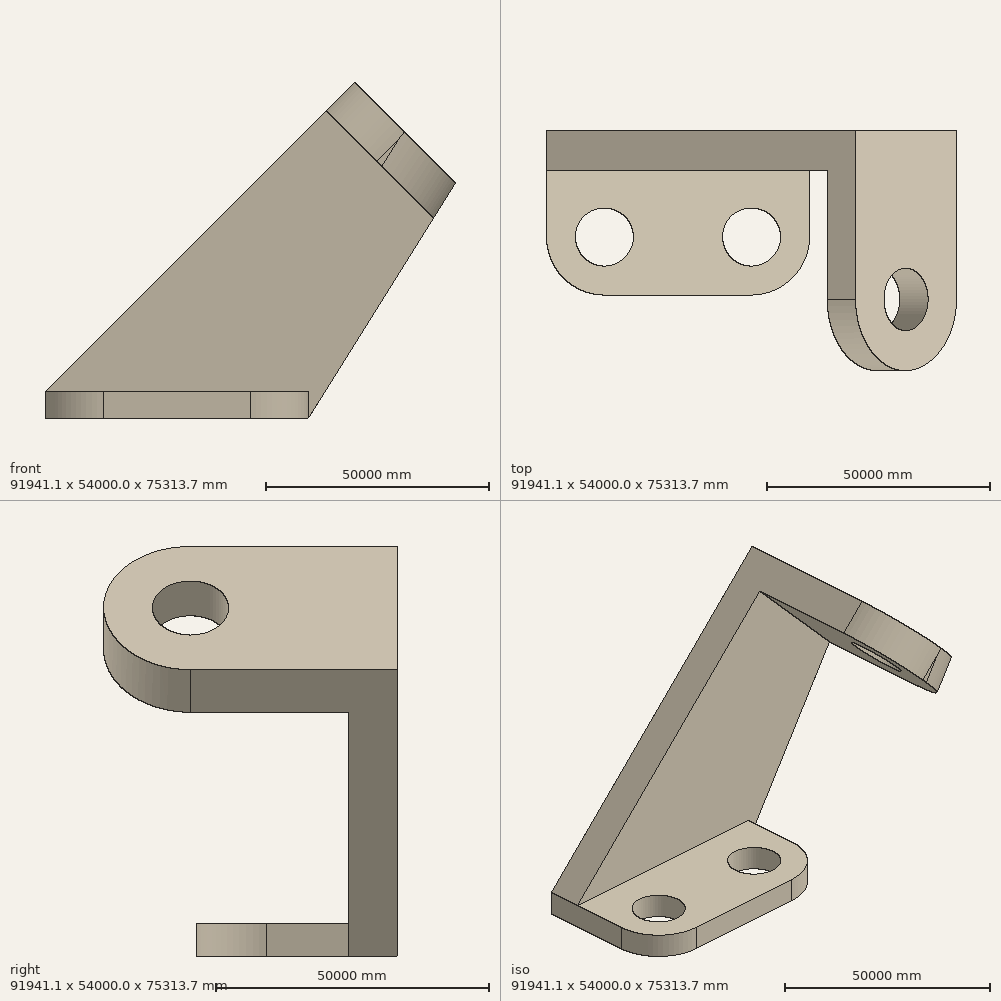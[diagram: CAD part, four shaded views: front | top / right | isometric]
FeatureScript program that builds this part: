
annotation { "Feature Type Name" : "Feature", "Feature Type Description" : "" }
export const myFeature = defineFeature(function(context is Context, id is Id, definition is map)
    precondition{}
    {
        {
            var Q0;
            Q0=qCreatedBy(makeId("Top.planeOp"),FACE);
            var sketch = newSketch(context, id + "F0", { "sketchPlane" : qUnion([Q0])});
            skLineSegment(sketch, "E0", {"start": v(0, 0) * mm, "end": v(59000, 0) * mm});
            skLineSegment(sketch, "E1", {"start": v(59000, 0) * mm, "end": v(59000, 37000) * mm});
            skLineSegment(sketch, "E2", {"start": v(59000, 37000) * mm, "end": v(0, 37000) * mm});
            skLineSegment(sketch, "E3", {"start": v(0, 37000) * mm, "end": v(0, 0) * mm});
            skSolve(sketch);
        }
        {
            var Q0;
            Q0 = qSketchRegion(id + "F0", true);
            extrude(context, id + "F1", {"entities" : qUnion([Q0]), "depth" : 6000 * mm});
        }
        {
            var Q0;
            Q0=makeQuery(id+"F1.opExtrude","SWEPT_EDGE",EDGE,{"disambiguationData":[OSD([sQuery(id+"F0.wireOp",EDGE,"E0"),sQuery(id+"F0.wireOp",EDGE,"E3")])]});
            var Q1;
            Q1=makeQuery(id+"F1.opExtrude","SWEPT_EDGE",EDGE,{"disambiguationData":[OSD([sQuery(id+"F0.wireOp",EDGE,"E0"),sQuery(id+"F0.wireOp",EDGE,"E1")])]});
            fillet(context, id + "F2", {"entities" : qUnion([Q0, Q1]), "radius" : 13000 * mm, "tangentPropagation" : true, "allowEdgeOverflow" : false});
        }
        {
            var Q0;
            Q0=makeQuery(id+"F1.opExtrude","SWEPT_FACE",FACE,{"disambiguationData":[OSD([sQuery(id+"F0.wireOp",EDGE,"E2")])]});
            var sketch = newSketch(context, id + "F3", { "sketchPlane" : qUnion([Q0])});
            skLineSegment(sketch, "E4", {"start": v(0, 6000) * mm, "end": v(-69313.7, 75313.7) * mm});
            skLineSegment(sketch, "E5", {"start": v(-69313.7, 75313.7) * mm, "end": v(-91941.13, 52686.3) * mm});
            skLineSegment(sketch, "E6", {"start": v(-91941.13, 52686.3) * mm, "end": v(-59000, 0) * mm});
            skPoint(sketch, "E7.endSnap0", {"position": v(-80627.42, 64000) * mm});
            skLineSegment(sketch, "E8", {"start": v(-80627.42, 64000) * mm, "end": v(-92777.93, 64000) * mm, "construction": true});
            skSolve(sketch);
        }
        {
            var Q0;
            Q0=makeQuery(id+"F3.imprint","IMPRINT",FACE,{"disambiguationData":[TD([[makeQuery(id+"F3.imprint","IMPRINT",EDGE,{"derivedFrom":sQuery(id+"F3.wireOp",EDGE,"E4")}),1.0]])]});
            extrude(context, id + "F4", {"entities" : qUnion([Q0]), "operationType" : NewBodyOperationType.ADD, "oppositeDirection" : true, "depth" : 9000 * mm});
        }
        {
            var Q0;
            Q0=makeQuery(id+"F1.opExtrude","CAP_FACE",FACE,{"disambiguationData":[OSD([sQuery(id+"F0.wireOp",EDGE,"E0"),sQuery(id+"F0.wireOp",EDGE,"E1"),sQuery(id+"F0.wireOp",EDGE,"E2"),sQuery(id+"F0.wireOp",EDGE,"E3")])],"isStart":false});
            var sketch = newSketch(context, id + "F5", { "sketchPlane" : qUnion([Q0])});
            skCircle(sketch, "E9", {"center": v(13000, 13000) * mm, "radius": 6500 * mm});
            skCircle(sketch, "E10", {"center": v(46000, 13000) * mm, "radius": 6500 * mm});
            skSolve(sketch);
        }
        {
            var Q0;
            Q0=makeQuery(id+"F5.imprint","IMPRINT",FACE,{"disambiguationData":[TD([[makeQuery(id+"F5.imprint","IMPRINT",EDGE,{"derivedFrom":sQuery(id+"F5.wireOp",EDGE,"E9")}),1.0]])]});
            var Q1;
            Q1=makeQuery(id+"F5.imprint","IMPRINT",FACE,{"disambiguationData":[TD([[makeQuery(id+"F5.imprint","IMPRINT",EDGE,{"derivedFrom":sQuery(id+"F5.wireOp",EDGE,"E10")}),1.0]])]});
            extrude(context, id + "F6", {"entities" : qUnion([Q0, Q1]), "operationType" : NewBodyOperationType.REMOVE, "oppositeDirection" : true, "depth" : 10000 * mm});
        }
        {
            var Q0;
            Q0=makeQuery(id+"F4.opExtrude","CAP_FACE",FACE,{"disambiguationData":[OSD([sQuery(id+"F0.wireOp",EDGE,"E1"),sQuery(id+"F0.wireOp",EDGE,"E2"),sQuery(id+"F3.wireOp",EDGE,"E4"),sQuery(id+"F3.wireOp",EDGE,"E5"),sQuery(id+"F3.wireOp",EDGE,"E6")])],"isStart":false});
            var sketch = newSketch(context, id + "F7", { "sketchPlane" : qUnion([Q0])});
            skLineSegment(sketch, "E11", {"start": v(69313.7, 75313.7) * mm, "end": v(62949.75, 68949.75) * mm});
            skLineSegment(sketch, "E12", {"start": v(62949.75, 68949.75) * mm, "end": v(87044.66, 44854.84) * mm});
            skLineSegment(sketch, "E13", {"start": v(87044.66, 44854.84) * mm, "end": v(91941.13, 52686.3) * mm});
            skLineSegment(sketch, "E14", {"start": v(91941.13, 52686.3) * mm, "end": v(69313.7, 75313.7) * mm});
            skSolve(sketch);
        }
        {
            var Q0;
            Q0=makeQuery(id+"F7.imprint","IMPRINT",FACE,{"disambiguationData":[TD([[makeQuery(id+"F7.imprint","IMPRINT",EDGE,{"derivedFrom":sQuery(id+"F7.wireOp",EDGE,"E11")}),-1.0]])]});
            extrude(context, id + "F8", {"entities" : qUnion([Q0]), "operationType" : NewBodyOperationType.ADD, "depth" : 45000 * mm});
        }
        {
            var Q0;
            Q0=makeQuery(id+"F8.opExtrude","CAP_EDGE",EDGE,{"disambiguationData":[OSD([sQuery(id+"F7.wireOp",EDGE,"E11")])],"isStart":false});
            var Q1;
            Q1=makeQuery(id+"F8.opExtrude","CAP_EDGE",EDGE,{"disambiguationData":[OSD([sQuery(id+"F7.wireOp",EDGE,"E13")])],"isStart":false});
            fillet(context, id + "F9", {"entities" : qUnion([Q0, Q1]), "radius" : 16000 * mm, "tangentPropagation" : true, "allowEdgeOverflow" : false});
        }
        {
            var Q0;
            Q0=makeQuery(id+"F8.boolean.opBoolean","MERGE",FACE,{"derivedFrom":[makeQuery(id+"F4.opExtrude","SWEPT_FACE",FACE,{"disambiguationData":[OSD([sQuery(id+"F3.wireOp",EDGE,"E5")])]}),makeQuery(id+"F8.opExtrude","SWEPT_FACE",FACE,{"disambiguationData":[OSD([sQuery(id+"F7.wireOp",EDGE,"E14")])]})]});
            var sketch = newSketch(context, id + "F10", { "sketchPlane" : qUnion([Q0])});
            skCircle(sketch, "E15", {"center": v(-1000, -11757.36) * mm, "radius": 7000 * mm});
            skSolve(sketch);
        }
        {
            var Q0;
            Q0 = qSketchRegion(id + "F10", true);
            extrude(context, id + "F11", {"entities" : qUnion([Q0]), "operationType" : NewBodyOperationType.REMOVE, "oppositeDirection" : true, "depth" : 10000 * mm});
        }
    });
